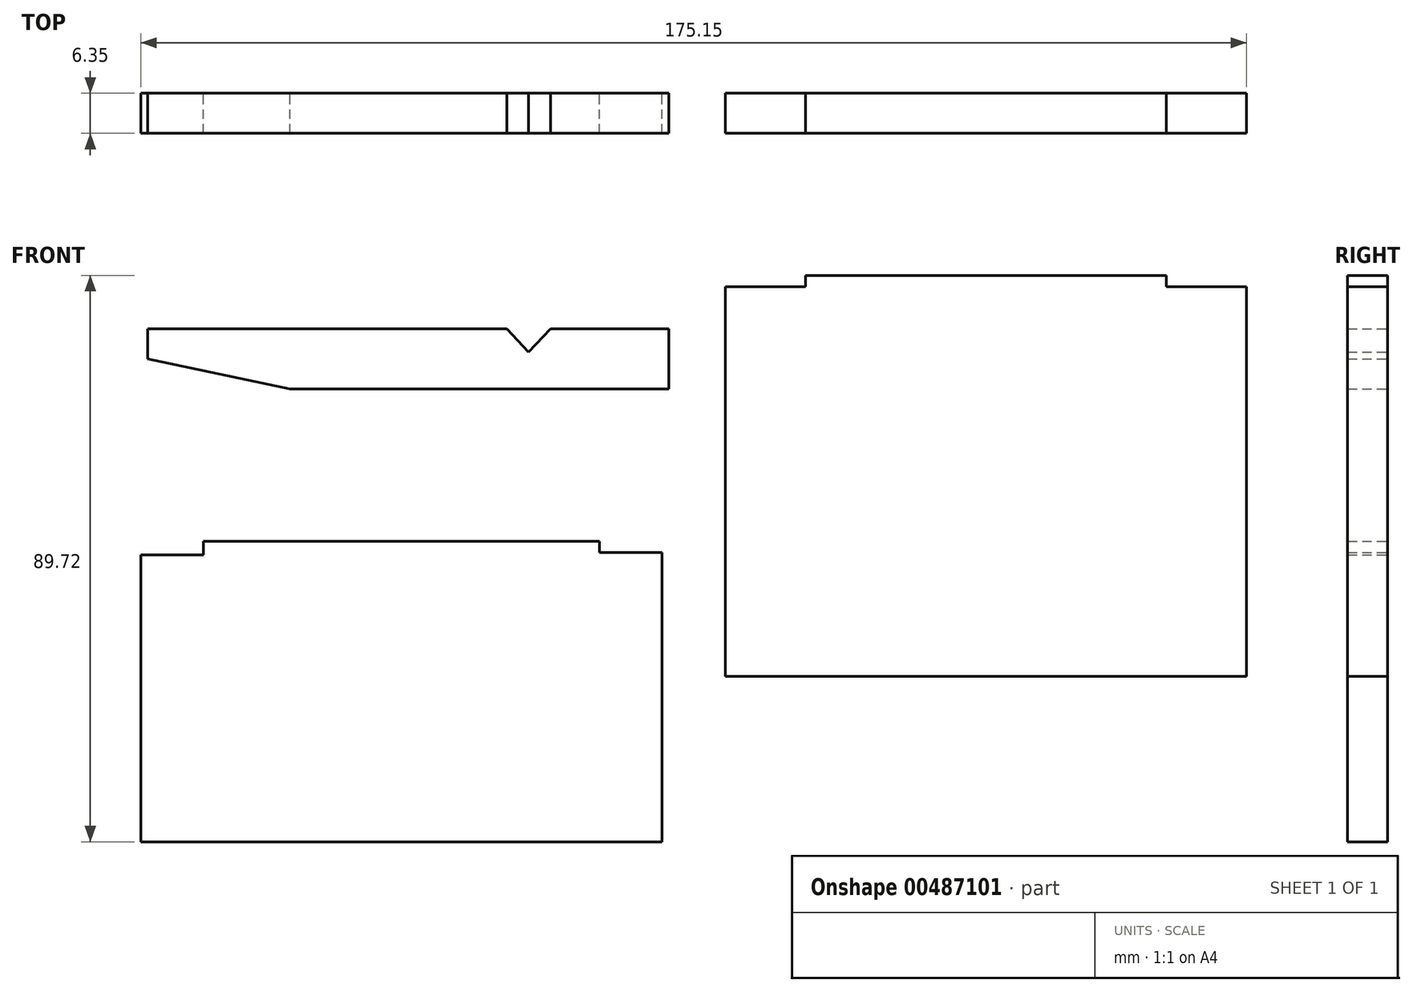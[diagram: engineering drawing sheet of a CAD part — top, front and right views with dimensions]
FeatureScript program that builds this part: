
annotation { "Feature Type Name" : "Feature", "Feature Type Description" : "" }
export const myFeature = defineFeature(function(context is Context, id is Id, definition is map)
    precondition{}
    {
        {
            var Q0;
            Q0=qCreatedBy(makeId("Front.planeOp"),FACE);
            var sketch = newSketch(context, id + "F0", { "sketchPlane" : qUnion([Q0])});
            skLineSegment(sketch, "E0.bottom", {"start": v(-31.37, 0) * mm, "end": v(31.37, 0) * mm});
            skLineSegment(sketch, "E0.top", {"start": v(-41.28, -47.63) * mm, "end": v(41.28, -47.63) * mm});
            skLineSegment(sketch, "E0.left", {"start": v(-41.28, -2.15) * mm, "end": v(-41.28, -47.63) * mm});
            skLineSegment(sketch, "E0.right", {"start": v(41.28, -1.78) * mm, "end": v(41.27, -47.63) * mm});
            skLineSegment(sketch, "E1.top", {"start": v(41.28, -1.78) * mm, "end": v(31.37, -1.78) * mm});
            skLineSegment(sketch, "E1.right", {"start": v(31.37, 0) * mm, "end": v(31.37, -1.78) * mm});
            skLineSegment(sketch, "E2.top", {"start": v(-41.28, -2.15) * mm, "end": v(-31.37, -2.15) * mm});
            skLineSegment(sketch, "E2.right", {"start": v(-31.37, 0) * mm, "end": v(-31.37, -2.15) * mm});
            skSolve(sketch);
        }
        {
            var Q0;
            Q0 = qSketchRegion(id + "F0", true);
            extrude(context, id + "F1", {"entities" : qUnion([Q0]), "depth" : 6.35 * mm});
        }
        {
            var Q0;
            Q0=qCreatedBy(makeId("Front.planeOp"),FACE);
            var sketch = newSketch(context, id + "F2", { "sketchPlane" : qUnion([Q0])});
            skLineSegment(sketch, "E3.bottom", {"start": v(-15.22, 42.1) * mm, "end": v(41.93, 42.1) * mm});
            skLineSegment(sketch, "E3.top", {"start": v(-27.92, -21.4) * mm, "end": v(54.63, -21.4) * mm});
            skLineSegment(sketch, "E3.left", {"start": v(-27.92, 40.32) * mm, "end": v(-27.92, -21.4) * mm});
            skLineSegment(sketch, "E3.right", {"start": v(54.63, 40.32) * mm, "end": v(54.63, -21.4) * mm});
            skLineSegment(sketch, "E4.top", {"start": v(-27.92, 40.32) * mm, "end": v(-15.22, 40.32) * mm});
            skLineSegment(sketch, "E4.right", {"start": v(-15.22, 42.1) * mm, "end": v(-15.22, 40.32) * mm});
            skLineSegment(sketch, "E5.top", {"start": v(54.63, 40.32) * mm, "end": v(41.93, 40.32) * mm});
            skLineSegment(sketch, "E5.right", {"start": v(41.93, 42.1) * mm, "end": v(41.93, 40.32) * mm});
            skSolve(sketch);
        }
        {
            var Q0;
            Q0 = qSketchRegion(id + "F2", true);
            extrude(context, id + "F3", {"entities" : qUnion([Q0]), "depth" : 6.35 * mm});
        }
        {
            var Q0;
            Q0=qCreatedBy(makeId("Front.planeOp"),FACE);
            var sketch = newSketch(context, id + "F4", { "sketchPlane" : qUnion([Q0])});
            skLineSegment(sketch, "E6", {"start": v(-40.18, 9.53) * mm, "end": v(16.68, 9.53) * mm});
            skLineSegment(sketch, "E7", {"start": v(42.37, 9.53) * mm, "end": v(42.37, 0) * mm});
            skPoint(sketch, "E8", {"position": v(20.15, 5.82) * mm});
            skLineSegment(sketch, "E9", {"start": v(16.68, 9.53) * mm, "end": v(20.15, 5.82) * mm});
            skLineSegment(sketch, "E10", {"start": v(23.62, 9.52) * mm, "end": v(20.15, 5.82) * mm});
            skLineSegment(sketch, "E11", {"start": v(-40.18, 9.53) * mm, "end": v(-40.18, 4.75) * mm});
            skLineSegment(sketch, "E12", {"start": v(42.37, 0) * mm, "end": v(-17.65, 0) * mm});
            skLineSegment(sketch, "E13", {"start": v(-17.65, 0) * mm, "end": v(-40.18, 4.75) * mm});
            skLineSegment(sketch, "E14.trimOffspring", {"start": v(23.62, 9.53) * mm, "end": v(42.37, 9.53) * mm});
            skSolve(sketch);
        }
        {
            var Q0;
            Q0 = qSketchRegion(id + "F4", true);
            extrude(context, id + "F5", {"entities" : qUnion([Q0]), "depth" : 6.35 * mm});
        }
        {
            var Q0;
            Q0=makeQuery(id+"F3.opExtrude","SWEPT_BODY",BODY,{"disambiguationData":[OSD([sQuery(id+"F2.wireOp",EDGE,"E3.bottom"),sQuery(id+"F2.wireOp",EDGE,"E3.top"),sQuery(id+"F2.wireOp",EDGE,"E3.left"),sQuery(id+"F2.wireOp",EDGE,"E3.right"),sQuery(id+"F2.wireOp",EDGE,"E4.top"),sQuery(id+"F2.wireOp",EDGE,"E4.right"),sQuery(id+"F2.wireOp",EDGE,"E5.top"),sQuery(id+"F2.wireOp",EDGE,"E5.right")])]});
            transform(context, id + "F6", {"entities" : qUnion([Q0]), "transformType" : TransformType.TRANSLATION_3D, "dx" : 79.25 * mm, "dy" : 0 * mm, "dz" : 0 * mm, "makeCopy" : false});
        }
        {
            var Q0;
            Q0=makeQuery(id+"F5.opExtrude","SWEPT_BODY",BODY,{"disambiguationData":[OSD([sQuery(id+"F4.wireOp",EDGE,"E6"),sQuery(id+"F4.wireOp",EDGE,"E7"),sQuery(id+"F4.wireOp",EDGE,"E9"),sQuery(id+"F4.wireOp",EDGE,"E10"),sQuery(id+"F4.wireOp",EDGE,"E11"),sQuery(id+"F4.wireOp",EDGE,"E12"),sQuery(id+"F4.wireOp",EDGE,"E13"),sQuery(id+"F4.wireOp",EDGE,"E14.trimOffspring")])]});
            transform(context, id + "F7", {"entities" : qUnion([Q0]), "transformType" : TransformType.TRANSLATION_3D, "dx" : 0 * mm, "dy" : 0 * mm, "dz" : 24.13 * mm, "makeCopy" : false});
        }
    });
